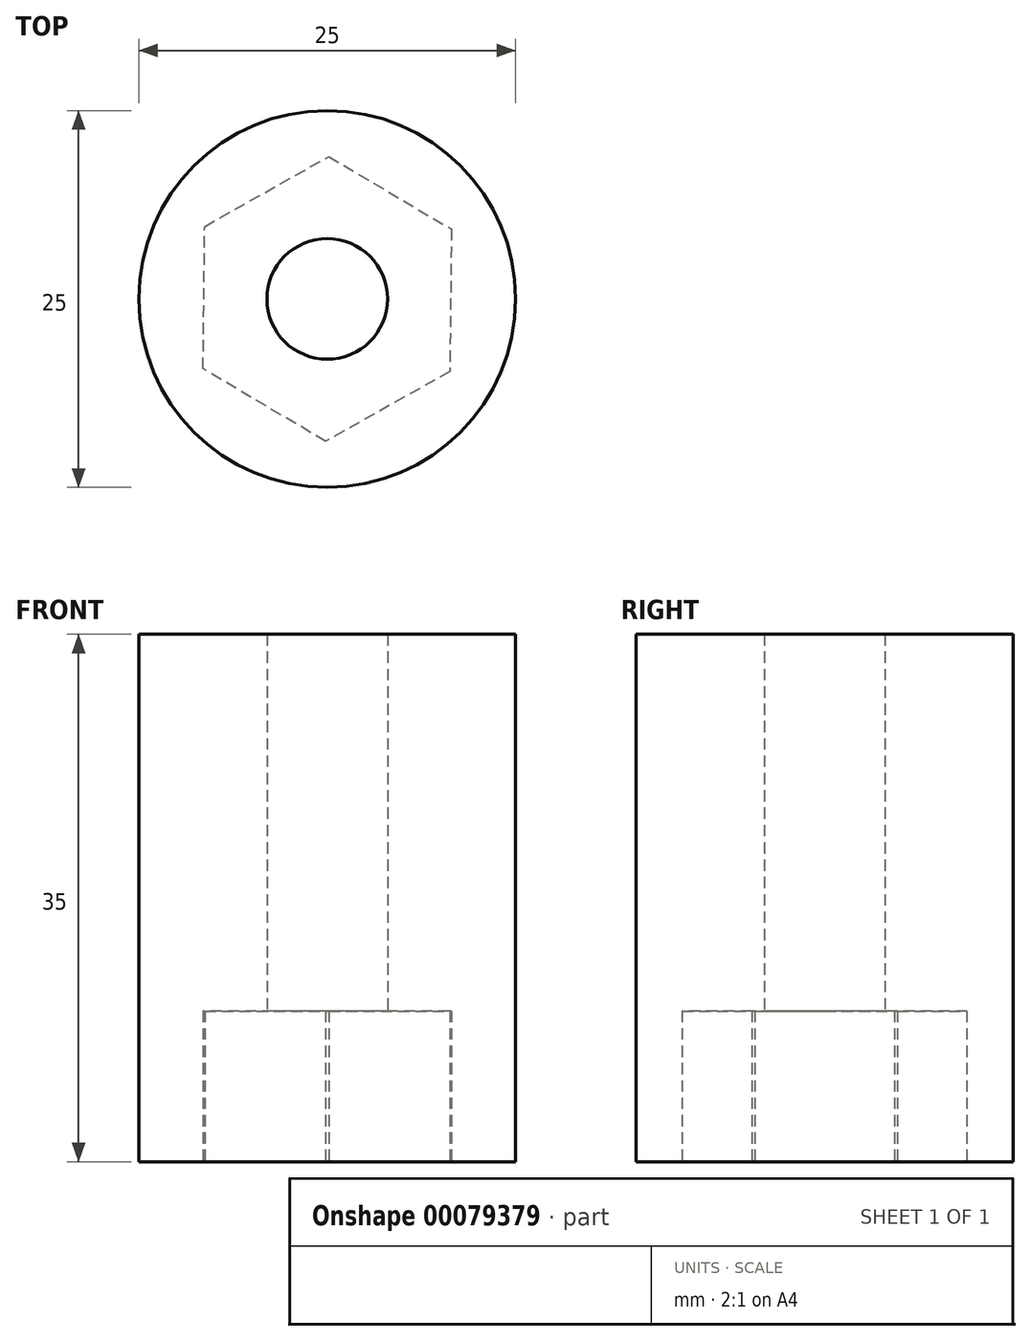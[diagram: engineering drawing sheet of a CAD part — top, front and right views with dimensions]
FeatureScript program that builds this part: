
annotation { "Feature Type Name" : "Feature", "Feature Type Description" : "" }
export const myFeature = defineFeature(function(context is Context, id is Id, definition is map)
    precondition{}
    {
        {
            var Q0;
            Q0=qCreatedBy(makeId("Top.planeOp"),FACE);
            var sketch = newSketch(context, id + "F0", { "sketchPlane" : qUnion([Q0])});
            skCircle(sketch, "E0.cCircle", {"center": v(-25.4, 4.92) * mm, "radius": 8.18 * mm, "construction": true});
            skLineSegment(sketch, "E0.0", {"start": v(-17.27, 0.1) * mm, "end": v(-25.5, -4.53) * mm});
            skLineSegment(sketch, "E0.1", {"start": v(-25.5, -4.53) * mm, "end": v(-33.63, 0.29) * mm});
            skLineSegment(sketch, "E0.2", {"start": v(-33.63, 0.29) * mm, "end": v(-33.53, 9.74) * mm});
            skLineSegment(sketch, "E0.3", {"start": v(-33.53, 9.74) * mm, "end": v(-25.3, 14.37) * mm});
            skLineSegment(sketch, "E0.4", {"start": v(-25.3, 14.37) * mm, "end": v(-17.16, 9.55) * mm});
            skLineSegment(sketch, "E0.5", {"start": v(-17.16, 9.55) * mm, "end": v(-17.27, 0.1) * mm});
            skPoint(sketch, "E0.0.midPoint", {"position": v(-21.38, -2.21) * mm});
            skCircle(sketch, "E1", {"center": v(-25.4, 4.92) * mm, "radius": 5 * mm});
            skCircle(sketch, "E2", {"center": v(-25.4, 4.92) * mm, "radius": 12.5 * mm});
            skSolve(sketch);
        }
        {
            var Q0;
            Q0=makeQuery(id+"F0.imprint","IMPRINT",FACE,{"disambiguationData":[TD([[makeQuery(id+"F0.imprint","IMPRINT",EDGE,{"derivedFrom":sQuery(id+"F0.wireOp",EDGE,"E0.0")}),1.0]])]});
            extrude(context, id + "F1", {"entities" : qUnion([Q0]), "depth" : 10 * mm});
        }
        {
            var Q0;
            Q0=makeQuery(id+"F1.opExtrude","CAP_FACE",FACE,{"disambiguationData":[OSD([sQuery(id+"F0.wireOp",EDGE,"E0.0"),sQuery(id+"F0.wireOp",EDGE,"E0.1"),sQuery(id+"F0.wireOp",EDGE,"E0.2"),sQuery(id+"F0.wireOp",EDGE,"E0.3"),sQuery(id+"F0.wireOp",EDGE,"E0.4"),sQuery(id+"F0.wireOp",EDGE,"E0.5"),sQuery(id+"F0.wireOp",EDGE,"E2")])],"isStart":false});
            var sketch = newSketch(context, id + "F2", { "sketchPlane" : qUnion([Q0])});
            skCircle(sketch, "E3", {"center": v(-25.4, 4.92) * mm, "radius": 12.5 * mm});
            skPoint(sketch, "E3.first.point", {"position": v(-37.8, 3.33) * mm});
            skPoint(sketch, "E3.second.point", {"position": v(-19.4, 15.9) * mm});
            skPoint(sketch, "E3.third.point", {"position": v(-16.34, -3.69) * mm});
            skCircle(sketch, "E4", {"center": v(-25.4, 4.92) * mm, "radius": 4 * mm});
            skSolve(sketch);
        }
        {
            var Q0;
            Q0=makeQuery(id+"F2.imprint","IMPRINT",FACE,{"disambiguationData":[TD([[makeQuery(id+"F2.imprint","IMPRINT",EDGE,{"derivedFrom":sQuery(id+"F2.wireOp",EDGE,"E4")}),-1.0]])]});
            var Q1;
            Q1=makeQuery(id+"F2.imprint","IMPRINT",FACE,{"disambiguationData":[TD([[makeQuery(id+"F2.imprint","IMPRINT",EDGE,{"derivedFrom":sQuery(id+"F2.wireOp",EDGE,"E3")}),1.0]])]});
            extrude(context, id + "F3", {"entities" : qUnion([Q0, Q1]), "operationType" : NewBodyOperationType.ADD, "depth" : 25 * mm});
        }
    });
